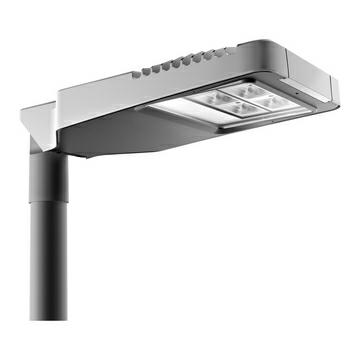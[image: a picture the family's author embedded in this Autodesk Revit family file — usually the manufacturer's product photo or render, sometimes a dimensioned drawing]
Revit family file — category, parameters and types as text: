
# Revit family: Lighting-StreetLighting-GEWISS-ROAD[5]MINI-LED_OPTIC_CYCLE-PEDESTRIAN_CLII
name_source: partatom
category: Apparecchi per illuminazione
units: mm (PartAtom-declared; Revit-internal decimal feet)

## family parameters
Basato su piano di lavoro = No
Condiviso = No
Punto di calcolo locali = No
Quota connettore circolare = Usa diametro
Sempre verticale = Sì
Sorgente d'illuminazione = No
Taglio con vuoti quando caricato = No
Tipo di parte = Normale

## types (6) — shared parameters
Applicazione = External
Catalogue = LIGHTING
Catalogue Range = ROAD [5]
Electrocod = 244C
IDF = 17b041e8-db93-43f8-8dc1-ed232e2b9226
IDT = 2f5e6c6e66cc494da4ced8a5a577b619
IP degree = IP66
Immagine tipo = GWR5276M.jpg
Insulation class = II
LED current. = 0,7A
Lamp- = LED
Lampada = LED
Minimum distance from the illuminated object = 1M
Produttore = GEWISS S.p.A.
SEO = Street lighting
Shock resistance = IK08
Technical sheet = https://www.gewiss.com
Tilt adjustable = -20° ÷ +10° side bracket - -10° ÷ +20° pole head
URL = https://www.gewiss.com
Version file RFA = 20.11
Warranty = 5 years

## per-type parameters (varying)
- GWR5371M30K - ROAD5 MINI CYCL 1M 3000K 0,7A CL2 1-10V: Body=Die-cast aluminium -; Classification:=-; Color Rendering Index=CRI-70; Colore=Graphite grey; Colour :=Powder coating; Colour temperature=3000K; Colour temperature:=3000 K (CRI>80); Context=Street and parking lighting; Control System=Dimmable 1-10 V; DIN 18032-3 certification=-; Descrizione=GWR5371M30K - ROAD5 MINI CYCL 1M 3000K 0,7A CL2 1-10V; Device with reduced surface temperature=-; Driver=Included; Driver Box=Built-in; Efficiency (lm/W)=70; Eletrical and lighting features=-; External screw=Stainless steel; Fixing=Pole Head - Outreach; Gasket=Anti-aging silicone; General information=-; Glow Wire Test :=-; IPEA=ROAD = C // LARGE AREAS = B // CYCLOPEDONALS = C // GREEN AREAS = C // HISTORICAL CENTER = A; Installationa and maintenance=-; LED Life Time (L80B05)=77000H; LED Maintenance=Not available; Lifetime=L90B10 (Tq+25°C) = 100.000 h - L90B10 (Tq+50°C) = 75.000 h; Locking Hook=Integrated front handle; Lumen output (lm)=1900; Luminaire=LED Road Equipment; Materials=-; Maximum surface exposed to the wind=0,149999999999999M2; Maximum surface exposed to the wind :=0.15 m²; Modello=GWR5371M30K; Mouting and installation=Pole Head - Outreach; Nominal flux (lm)=2045; Number of modules=1 (1x3 LED); Operating temperature :=-25 +50 °C; Operating temperature:=-25 +50 °C; Optic=CYCLE; Optic :=Metallized polycarbonate reflector; Optic Maintenance=Not available; Optic and illuminating features=-; Overvoltage protection=DM 10KV / CM 10KV; Overvoltage resistance :=Common and dfferential mode: 10KV; Photobiological Risk Class=RG0; Power supply operation=Dimmable; Rated frequency (Hz)=50 / 60; Shield type=4mm thick flat tempered glass; Standard Deviation Colour Matching=SDCM = 5; Standard-=EN 60598-2-3, EN 60598-1 IEC/TR 62778; Standards and approvals=-; Stocking temperature=-; Supply voltage=220 - 240 V; System power=27W; System power :=27 W @ 0.7A; Tilt-=-20° ÷ +10° side bracket - -10° ÷ +20° pole head; Tipo alimentatore=Constant Current Driver Led; Tipologia=Dimmable; Type of light source=LED - Not replaceable; Unified Glare Rating=G*3 - ULOR = 0; Unique digital code (Datamatrix)=Currently not present; Voltage-=220/240 V - 50/60 Hz - Dimmable 1-10 V; Weight (kg):=6,4; Wiring=Isolating switch
- GWR5372M - ROAD5 MINI CYCL 2M 4000K 0,7A CL2 1-10V: Colour temperature=4000 K (CRI 70); Colour temperature:=4000 K (CRI 70); Descrizione=ROAD5 MINI CYCL 2M 4000K 0,7A CL2 1-10V; EAN code=8011564885325; LED LifeTime (L80B05)=77000H; Lumen output (lm)=3800; Maximum surface exposed to the wind=0,15M2; Modello=GWR5372M; No. Chorus modules=2 (2x3 LED); Nominal flux (lm)=4700; Number of modules=2 (2x3 LED); Operating temperature:=-25 +50 °C; Optic=Cycle and pedestrian - ULOR: 0%; Overvoltage resistance=12 KV (Common and dfferential mode); Pilot current=0,7A; Power supply operation=Dimmable; System power=53W; Tipo alimentatore=Constant Current Driver Led; Tipologia=Dimmable; Voltage-=220/240 V - 50/60 Hz - Dimmable 1-10 V; Weight (kg)=6,6; Weight (kg):=6,6; Working temperature=-25 +50 °C
- GWR5371M - ROAD5 MINI CYCL 1M 4000K 0,7A CL2 1-10V: Colour temperature=4000 K (CRI 70); Colour temperature:=4000 K (CRI 70); Descrizione=ROAD5 MINI CYCL 1M 4000K 0,7A CL2 1-10V; EAN code=8011564885318; LED LifeTime (L80B05)=77000H; Lumen output (lm)=1900; Maximum surface exposed to the wind=0,15M2; Modello=GWR5371M; No. Chorus modules=1 (1x3 LED); Nominal flux (lm)=2350; Number of modules=1 (1x3 LED); Operating temperature:=-25 +50 °C; Optic=Cycle and pedestrian - ULOR: 0%; Overvoltage resistance=12 KV (Common and dfferential mode); Pilot current=0,7A; Power supply operation=Dimmable; System power=27W; Tipo alimentatore=Constant Current Driver Led; Tipologia=Dimmable; Voltage-=220/240 V - 50/60 Hz - Dimmable 1-10 V; Weight (kg)=6,4; Weight (kg):=6,4; Working temperature=-25 +50 °C
- GWR5372M30K - ROAD5 MINI CYCL 2M 3000K 0,7A CL2 1-10V: Body=Die-cast aluminium -; Classification:=-; Color Rendering Index=CRI-70; Colore=Graphite grey; Colour :=Powder coating; Colour temperature=3000K; Colour temperature:=3000 K (CRI>80); Context=Street and parking lighting; Control System=Dimmable 1-10 V; DIN 18032-3 certification=-; Descrizione=GWR5372M30K - ROAD5 MINI CYCL 2M 3000K 0,7A CL2 1-10V; Device with reduced surface temperature=-; Driver=Included; Driver Box=Built-in; Efficiency (lm/W)=72; Eletrical and lighting features=-; External screw=Stainless steel; Fixing=Pole Head - Outreach; Gasket=Anti-aging silicone; General information=-; Glow Wire Test :=-; IPEA=ROAD = C // LARGE AREAS = B // CYCLOPEDONALS = C // GREEN AREAS = C // HISTORICAL CENTER = A; Installationa and maintenance=-; LED Life Time (L80B05)=77000H; LED Maintenance=Not available; Lifetime=L90B10 (Tq+25°C) = 100.000 h - L90B10 (Tq+50°C) = 75.000 h; Locking Hook=Integrated front handle; Lumen output (lm)=3800; Luminaire=LED Road Equipment; Materials=-; Maximum surface exposed to the wind=0,149999999999999M2; Maximum surface exposed to the wind :=0.15 m²; Modello=GWR5372M30K; Mouting and installation=Pole Head - Outreach; Nominal flux (lm)=4090; Number of modules=2 (2x3 LED); Operating temperature :=-25 +50 °C; Operating temperature:=-25 +50 °C; Optic=CYCLE; Optic :=Metallized polycarbonate reflector; Optic Maintenance=Not available; Optic and illuminating features=-; Overvoltage protection=DM 10KV / CM 10KV; Overvoltage resistance :=Common and dfferential mode: 10KV; Photobiological Risk Class=RG0; Power supply operation=Dimmable; Rated frequency (Hz)=50 / 60; Shield type=4mm thick flat tempered glass; Standard Deviation Colour Matching=SDCM = 5; Standard-=EN 60598-2-3, EN 60598-1 IEC/TR 62778; Standards and approvals=-; Stocking temperature=-; Supply voltage=220 - 240 V; System power=53W; System power :=53 W @ 0.7A; Tilt-=-20° ÷ +10° side bracket - -10° ÷ +20° pole head; Tipo alimentatore=Constant Current Driver Led; Tipologia=Dimmable; Type of light source=LED - Not replaceable; Unified Glare Rating=G*3 - ULOR = 0; Unique digital code (Datamatrix)=Currently not present; Voltage-=220/240 V - 50/60 Hz - Dimmable 1-10 V; Weight (kg):=6,59999999999999; Wiring=Isolating switch
- GWR5372MV - ROAD5 MINI CYC.V 2M 4000K 0,7A CL2: Body=Die-cast aluminium -; Classification:=-; Color Rendering Index=CRI-70; Colore=Graphite grey; Colour :=Powder coating; Colour temperature=4000K; Colour temperature:=4000 K (CRI>70); Context=Street and parking lighting; Control System=DALI - 5 Step; DIN 18032-3 certification=-; Descrizione=GWR5372MV - ROAD5 MINI CYC.V 2M 4000K 0,7A CL2; Device with reduced surface temperature=-; Driver=Included; Driver Box=Built-in; Efficiency (lm/W)=72; Eletrical and lighting features=-; External screw=Stainless steel; Fixing=Pole Head - Outreach; Gasket=Anti-aging silicone; General information=-; Glow Wire Test :=-; IPEA=ROAD = C // LARGE AREAS = B // CYCLOPEDONALS = C // GREEN AREAS = C // HISTORICAL CENTER = A; Installationa and maintenance=-; LED Life Time (L80B05)=120000H; LED Maintenance=Not available; Lifetime=L90B10 (Tq+25°C) = 100.000 h - L90B10 (Tq+50°C) = 75.000 h; Locking Hook=Integrated front handle; Lumen output (lm)=3800; Luminaire=LED Road Equipment; Materials=-; Maximum surface exposed to the wind=0,19M2; Maximum surface exposed to the wind :=0.15 m²; Modello=GWR5372MV; Mouting and installation=Pole Head - Outreach; Nominal flux (lm)=4700; Number of modules=2 (2x3 LED); Operating temperature :=-25 +50 °C; Operating temperature:=-25 +40 °C; Optic=CYCLE; Optic :=Metallized polycarbonate reflector; Optic Maintenance=Not available; Optic and illuminating features=-; Overvoltage protection=DM 10KV / CM 10KV; Photobiological Risk Class=RG0; Rated frequency (Hz)=50 / 60; Shield type=4mm thick flat tempered glass; Standard Deviation Colour Matching=SDCM = 5; Standard-=EN 60598-2-3, EN 60598-1 IEC/TR 62778; Standards and approvals=-; Stocking temperature=-; Supply voltage=220 - 240 V; System power=53W; System power :=53 W @ 0.7A; Tilt-=-20° ÷ +10° side bracket - -10° ÷ +20° pole head; Tipologia=Programmable (5 step); Type of light source=LED - Not replaceable; Unified Glare Rating=G*3 - ULOR = 0; Unique digital code (Datamatrix)=Currently not present; Voltage-=220/240 V - 50/60 Hz - Stand alone and/or programmable; Weight (kg):=6,6; Wiring=Isolating switch
- GWR5371MV - ROAD5 MINI CYC.V 1M 4000K 0,7A CL2: Body=Die-cast aluminium -; Classification:=-; Color Rendering Index=CRI-70; Colore=Graphite grey; Colour :=Powder coating; Colour temperature=4000K; Colour temperature:=4000 K (CRI>70); Context=Street and parking lighting; Control System=DALI - 5 Step; DIN 18032-3 certification=-; Descrizione=GWR5371MV - ROAD5 MINI CYC.V 1M 4000K 0,7A CL2; Device with reduced surface temperature=-; Driver=Included; Driver Box=Built-in; Efficiency (lm/W)=70; Eletrical and lighting features=-; External screw=Stainless steel; Fixing=Pole Head - Outreach; Gasket=Anti-aging silicone; General information=-; Glow Wire Test :=-; IPEA=ROAD = C // LARGE AREAS = B // CYCLOPEDONALS = C // GREEN AREAS = C // HISTORICAL CENTER = A; Installationa and maintenance=-; LED Life Time (L80B05)=120000H; LED Maintenance=Not available; Lifetime=L90B10 (Tq+25°C) = 100.000 h - L90B10 (Tq+50°C) = 75.000 h; Locking Hook=Integrated front handle; Lumen output (lm)=1900; Luminaire=LED Road Equipment; Materials=-; Maximum surface exposed to the wind=0,19M2; Maximum surface exposed to the wind :=0.15 m²; Modello=GWR5371MV; Mouting and installation=Pole Head - Outreach; Nominal flux (lm)=2350; Number of modules=1 (1x3 LED); Operating temperature :=-25 +50 °C; Operating temperature:=-25 +40 °C; Optic=CYCLE; Optic :=Metallized polycarbonate reflector; Optic Maintenance=Not available; Optic and illuminating features=-; Overvoltage protection=DM 10KV / CM 10KV; Photobiological Risk Class=RG0; Rated frequency (Hz)=50 / 60; Shield type=4mm thick flat tempered glass; Standard Deviation Colour Matching=SDCM = 5; Standard-=EN 60598-2-3, EN 60598-1 IEC/TR 62778; Standards and approvals=-; Stocking temperature=-; Supply voltage=220 - 240 V; System power=27W; System power :=27 W @ 0.7A; Tilt-=-20° ÷ +10° side bracket - -10° ÷ +20° pole head; Tipologia=Programmable (5 step); Type of light source=LED - Not replaceable; Unified Glare Rating=G*3 - ULOR = 0; Unique digital code (Datamatrix)=Currently not present; Voltage-=220/240 V - 50/60 Hz - Stand alone and/or programmable; Weight (kg):=6,4; Wiring=Isolating switch

## geometry (parser evidence)
native form markers: Blend x2
no freeform markers — native parametric forms only
